# Revit family: (VRO) Vicky Ring Outward Light Acoustic Light
name_source: partatom
category: Lighting Fixtures
units: mm (PartAtom-declared; Revit-internal decimal feet)

## family parameters
Cut with Voids When Loaded = No
Host = Face
Light Source = Yes
Part Type = Normal
Room Calculation Point = No
Round Connector Dimension = Use Diameter
Shared = No

## types (7) — shared parameters
A = 0' - 5"
A1 = 0' - 3 1/2"
Average life based on 77F(HRS) = 50000
B = 0' - 1 3/8"
C = 0' - 1 13/32"
CRI = 90
Color Filter = 16777215
Description = The Vicky Ring light is a unique ring style light with an LED light source illuminating from its outer surface.
Dimming / Control = 0-10 V
Dimming Lamp Color Temperature Shift = <None>
H = 0' - 1 5/16"
H2 = 3' - 10 5/8"
IP Rating = 20
Load Classification = Lighting
Manufacturer = Above All Lighting
Power Factor = 1
Suspender Height = 4' - 0"
Tilt Angle = -90.00°
Type Comments = Ring Outward Light Acoustic Light
URL = https://www.abovealllighting.com
Voltage = 120-277 V

## per-type parameters (varying)
| type | Apparent Load | D | D1 | D2 | D3 | Default Elevation | Finish/Color | H1 | Inner Diameter | Inside Body Material | Model | Order number | Photometric Web File | Wattage Comments |
| VRO-3624-40901-ACPMK-WH | 40 VA | 1' - 11 19/32" | 0' - 11 13/16" | 0' - 11 5/16" | 0' - 7 13/16" | 0' - 0" | White | 3' - 11 9/32" | 0' - 10 1/2" | <By Category> | VRO-3624-40901-ACPMK-WH | 16275 | VRO-3624-40901-WH.ies | 32 W |
| VRO-4035-30901-ACPMK-WH | 50 VA | 2' - 11 13/32" | 1' - 5 11/16" | 1' - 5 3/16" | 1' - 1 11/16" | 4' - 0" | White | 4' - 0 19/32" | 1' - 4 13/32" | <By Category> | VRO-4035-40901-ACPMK-WH | 16276 | VRO_4035_30901_WH.ies | 40 W |
| VRO-7047-30901-ACPMK-WH | 88 VA | 3' - 11 7/32" | 1' - 11 19/32" | 1' - 11 3/32" | 1' - 7 19/32" | 0' - 0" | White | 4' - 2 9/16" | 1' - 10 5/16" | <By Category> | VRO-7047-40901-ACPMK-WH | 16277 | VRO_7047_30901_WH.ies | 70 W |
| VRO-8059-30901-ACPMK-WH | 100 VA | 4' - 11 3/32" | 2' - 5 9/16" | 2' - 5 1/16" | 2' - 1 9/16" | 0' - 0" | Alluminium Fiber | 4' - 5 5/32" | 2' - 4 1/4" | <By Category> | VRO-8059-40901-ACPMK-WH | 16278 | VRO_8059_30901_WH.ies | 80 W |
| VRO-LA-3624-40901-ACPMK-WH-NSAC-021 130 | 40 VA | 1' - 11 19/32" | 0' - 11 13/16" | 0' - 11 5/16" | 0' - 7 13/16" | 0' - 0" | Alluminium Fiber | 3' - 11 9/32" | 0' - 10 1/2" | Acoustic -130 | VRO-LA-3624-40901-ACPMK-WH-NSAC-021 130 | 16283 | VRO_LA_3624_XX901_with_acoustic.ies | 32 W |
| VRO-LA-4035-40901-ACPMK-WH-NSAC-021 130 | 50 VA | 2' - 11 13/32" | 1' - 5 11/16" | 1' - 5 3/16" | 1' - 1 11/16" | 0' - 0" | Alluminium Fiber | 4' - 0 19/32" | 1' - 4 13/32" | Acoustic -130 | VRO-LA-4035-40901-ACPMK-WH-NSAC-021 130 | 16284 | VRO_LA_4035_XX901_with_acoustic.ies | 40 W |
| VRO-LA-7047-40901-ACPMK-WH-NSAC-021 130 | 88 VA | 3' - 11 7/32" | 1' - 11 19/32" | 1' - 11 3/32" | 1' - 7 19/32" | 0' - 0" | Alluminium Fiber | 4' - 2 9/16" | 1' - 10 5/16" | Acoustic -130 | VRO-LA-7047-40901-ACPMK-WH-NSAC-021 130 | 16285 | VRO_LA_7047_XX901_with_acoustic.ies | 70 W |

## geometry (parser evidence)
native form markers: Sweep x8
no freeform markers — native parametric forms only
